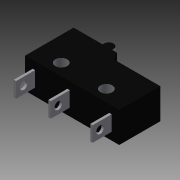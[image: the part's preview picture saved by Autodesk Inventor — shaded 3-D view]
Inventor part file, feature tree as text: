
AUTODESK INVENTOR PART (.ipt)
format: ipt  version: 2013 (Build 170138000, 138)  size: 143,360 bytes
history: native  units: mm
features: extrude x4, sketch x4
ambient origin geometry x8: Origin, YZ Plane, XZ Plane, XY Plane, X Axis, Y Axis, Z Axis, Center Point
bodies: Solid1 (feature_tree)
feature tree (8):
  extrude  "Extrusion1"  Depth=6.4mm TaperAngle=0.0deg
  extrude  "Extrusion3"  Depth=6.4mm TaperAngle=0.0deg
  extrude  "Extrusion4"  Depth=1.6mm
  extrude  "Extrusion2"  [1 undecoded]
  sketch  "Sketch1"  dims[d0=9.1mm d1=10.2mm d2=19.8mm d3=2.5mm d4=5.1mm d5=2.5mm d6=9.5mm d7=2.5mm d8=2.5mm d9=2.0mm d10=7.5mm d11=10.5mm d12=6.4mm d13=0.0mm]
  sketch  "Sketch2"  dims[d14=0.5mm d15=4.0mm d16=0.5mm d17=0.5mm d18=8.3mm d19=6.8mm d20=6.4mm d21=0.0mm]
  sketch  "Sketch3"  dims[d22=4.0mm d23=0.0mm d24=1.6mm]
  sketch  "Sketch4"  dims[d26=22.0mm d27=0.0mm]
note: 1 required parameter value undecoded (feature->parameter linkage not recoverable at this tier; creation-order binding heuristic only, values carry confidence <= 0.55)
